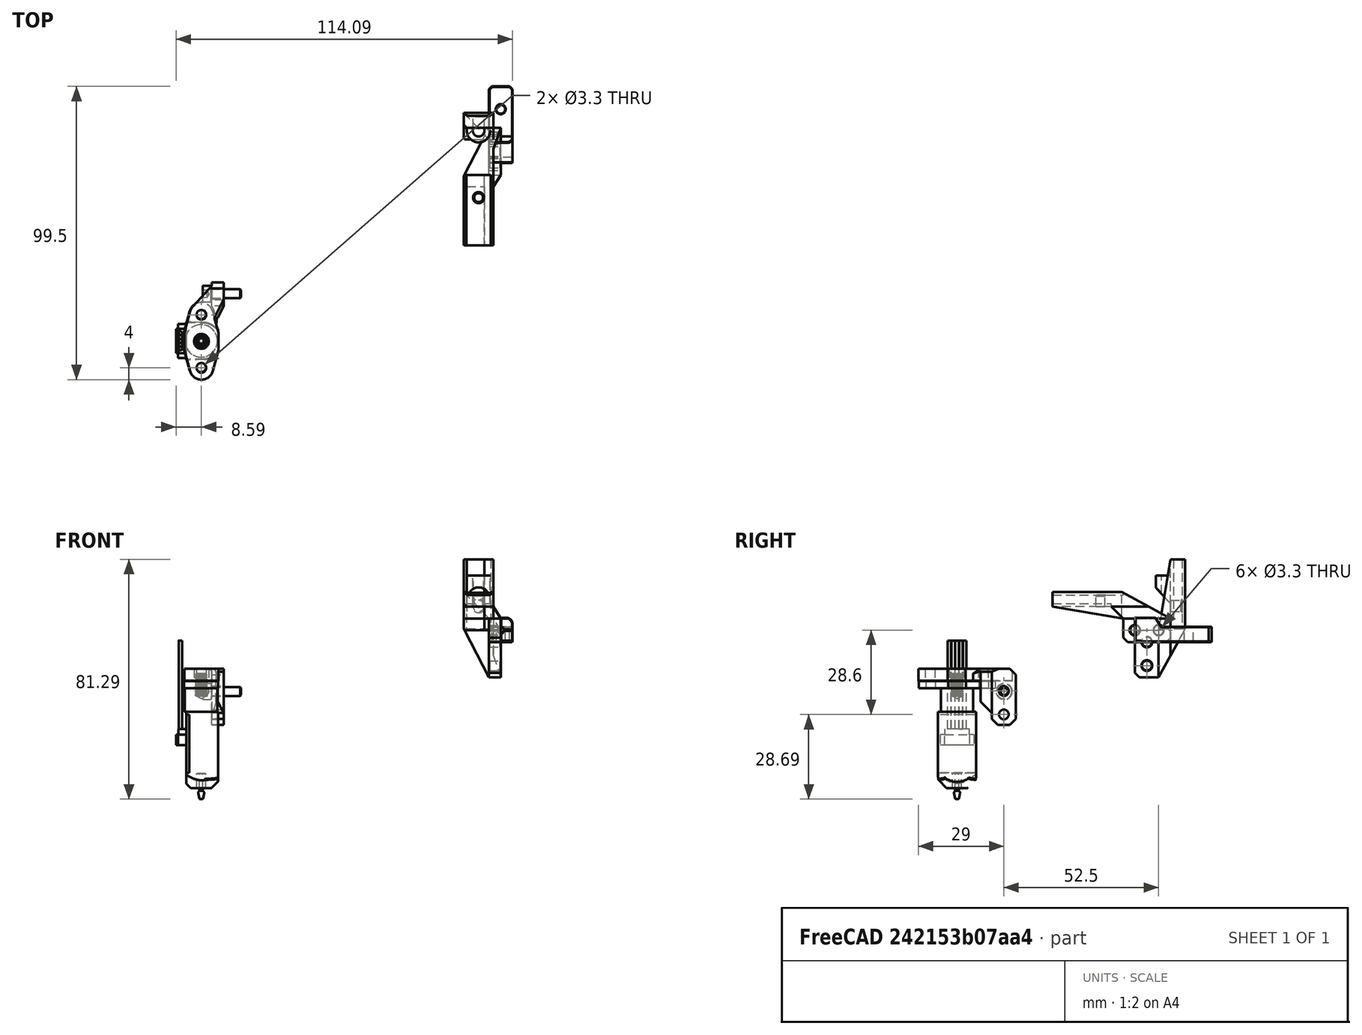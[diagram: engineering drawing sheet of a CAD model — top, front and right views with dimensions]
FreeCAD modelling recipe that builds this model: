
FCSTD DOCUMENT  (FreeCAD 0.19R24291 (Git))
Label: probe-mount-GXH8B
License: Other
LicenseURL: GPL3
objects: Part::Chamfer×18, Part::Box×14, Part::Cut×11, Part::Cylinder×5, Part::MultiFuse×5, Part::Feature×4, Part::FeaturePython×2, Part::Fillet×1, App::Part×1, Part::Refine×1
note: 61 computed .brp shape members not serialized (recipe doc carries the construction recipe); baked Part::Feature solids carry a one-line shape summary decoded from their .brp

FEATURE [Part::Box] Box  label="Cube"
  AttacherType = Attacher::AttachEngine3D
  Height = 8.2
  Length = 8
  Width = 9
FEATURE [Part::Box] Box001  label="Cube001"
  AttacherType = Attacher::AttachEngine3D
  Height = 5.2
  Length = 8
  Placement = pos=(0,8,0) rot=(0,0,1;0rad)
  Width = 18
FEATURE [Part::Box] Box002  label="Cube002"
  AttacherType = Attacher::AttachEngine3D
  Height = 0.2
  Length = 8
  Width = 2
FEATURE [Part::Cylinder] Cylinder
  Angle = 360
  AttacherType = Attacher::AttachEngine3D
  Height = 10
  Placement = pos=(4,18.25,0) rot=(0,0,1;0rad)
  Radius = 1.5
FEATURE [Part::Cylinder] Cylinder001
  Angle = 360
  AttacherType = Attacher::AttachEngine3D
  Height = 10
  Placement = pos=(4,0.25,4) rot=(1,0,0;1.5708rad)
  Radius = 1
FEATURE [Part::Box] Box003  label="Cube003"
  AttacherType = Attacher::AttachEngine3D
  Height = 2
  Length = 0.4
  Placement = pos=(3.8,0,0.5) rot=(0,0,1;0rad)
  Width = 0.25
FEATURE [Part::Box] Box004  label="Cube004"
  AttacherType = Attacher::AttachEngine3D
  Height = 2
  Length = 0.4
  Placement = pos=(3.8,0,5.5) rot=(0,0,1;0rad)
  Width = 0.25
FEATURE [Part::MultiFuse] Fusion001
  Shapes = -> [Box003,Box004]
FEATURE [Part::Feature] Fusion001001
  Placement = pos=(-1.8e-15,0,8) rot=(0,1,0;1.5708rad)
  shape: bbox 7 x 0.25 x 0.4 mm, 12 faces, 2 solids (baked)
FEATURE [Part::MultiFuse] Fusion001002
  Shapes = -> [Fusion001,Fusion001001]
FEATURE [Part::Cylinder] Cylinder002
  Angle = 360
  AttacherType = Attacher::AttachEngine3D
  Height = 10
  Placement = pos=(-1e-15,0,4) rot=(0,1,0;1.5708rad)
  Radius = 1.65
FEATURE [Part::Cylinder] Cylinder003
  Angle = 360
  AttacherType = Attacher::AttachEngine3D
  Height = 10
  Placement = pos=(-1e-15,8,4) rot=(0,1,0;1.5708rad)
  Radius = 1.65
FEATURE [Part::Box] Box007  label="Cube007"
  AttacherType = Attacher::AttachEngine3D
  Height = 8
  Length = 4
  Placement = pos=(0,-4,0) rot=(0,0,1;0rad)
  Width = 16
FEATURE [Part::Box] Box008  label="Cube008"
  AttacherType = Attacher::AttachEngine3D
  Height = 9
  Length = 12.5
  Placement = pos=(-8.5,-8,8) rot=(0,0,1;0rad)
  Width = 20
FEATURE [Part::Box] Box009  label="Cube009"
  AttacherType = Attacher::AttachEngine3D
  Height = 5
  Length = 10
  Placement = pos=(-8.5,-28,12) rot=(0,0,1;0rad)
  Width = 23.5
FEATURE [Part::Box] Box010  label="Cube010"
  AttacherType = Attacher::AttachEngine3D
  Height = 10
  Length = 12.5
  Placement = pos=(1.5,-9.5,8) rot=(0,0,1;0rad)
  Width = 21.5
FEATURE [Part::Chamfer] Chamfer009
  Base = -> Box010
  Edges = 1 edges: [Edge4 r1=4 r2=2.5]
FEATURE [Part::Chamfer] Chamfer010
  Base = -> Box008
  Edges = 1 edges r=4: [Edge9]
FEATURE [Part::Cut] Cut003001002
  Base = -> Chamfer010
  Tool = -> Chamfer009
FEATURE [Part::Chamfer] Chamfer011
  Base = -> Box007
  Edges = 2 edges r=1.5: [Edge9,Edge11]
FEATURE [Part::MultiFuse] Fusion001003
  Shapes = -> [Cylinder003,Cylinder002]
FEATURE [Part::Cut] Cut003001003
  Base = -> Chamfer011
  Tool = -> Fusion001003
FEATURE [Part::Box] Box011  label="Cube011"
  AttacherType = Attacher::AttachEngine3D
  Height = 5
  Length = 8.2
  Placement = pos=(-7.6,-28.5,16) rot=(0,0,1;0rad)
  Width = 24
FEATURE [Part::Chamfer] Chamfer012
  Base = -> Cut003001002
  Edges = 1 edges: [Edge4 r1=16.5 r2=8.5]
FEATURE [Part::Box] Box012  label="Cube012"
  AttacherType = Attacher::AttachEngine3D
  Height = 17
  Length = 15
  Placement = pos=(-10.8,-4.5,8) rot=(0,0,1;0rad)
  Width = 21
FEATURE [Part::Chamfer] Chamfer013
  Base = -> Box012
  Edges = 1 edges: [Edge9 r1=9 r2=16.5]
FEATURE [Part::Cut] Cut003001004
  Base = -> Chamfer012
  Tool = -> Chamfer013
FEATURE [Part::Box] Box013  label="Cube013"
  AttacherType = Attacher::AttachEngine3D
  Height = 5
  Length = 3
  Placement = pos=(-1.5,-3.5,13) rot=(1,0,0;3.14159rad)
  Width = 24.5
FEATURE [Part::Cylinder] Cylinder004
  Angle = 360
  AttacherType = Attacher::AttachEngine3D
  Height = 10
  Placement = pos=(-3.5,-12.25,10) rot=(0,0,1;0rad)
  Radius = 1.9
FEATURE [Part::Cut] Cut
  Base = -> Box
  Tool = -> Box002
FEATURE [Part::Chamfer] Chamfer
  Base = -> Cut
  Edges = 1 edges: [Edge10 r1=2 r2=3]
FEATURE [Part::Fillet] Fillet
  Base = -> Chamfer
  Edges = 2 edges r=2: [Edge1,Edge9]
FEATURE [Part::Chamfer] Chamfer001
  Base = -> Fillet
  Edges = 2 edges r=0.2: [Edge2,Edge16]
FEATURE [Part::Chamfer] Chamfer002
  Base = -> Chamfer001
  Edges = 2 edges r=0.2: [Edge5,Edge31]
FEATURE [Part::Cut] Cut001
  Base = -> Chamfer002
  Tool = -> Cylinder001
FEATURE [Part::Chamfer] Chamfer005
  Base = -> Cut001
  Edges = 9 edges r=0.2: [Edge4,Edge17,Edge19,Edge20,Edge21,Edge22,Edge23,Edge24,Edge25]
FEATURE [Part::Chamfer] Chamfer006
  Base = -> Chamfer005
  Edges = 5 edges r=0.2: [Edge7,Edge9,Edge14,Edge15,Edge16]
FEATURE [Part::Cut] Cut003001008
  Base = -> Chamfer006
  Tool = -> Fusion001002
FEATURE [Part::Feature] Part__Feature112001139  label="BL-touch v3.x002"
  Placement = pos=(-97.5942,-60.3565,-13.2887) rot=(0,0,1;1.5708rad)
  shape: bbox 16.53 x 26.01 x 53.81 mm, 111 faces (baked)
FEATURE [Part::FeaturePython] Screw1371  label="M3x10-Screw189"  # Fasteners workbench fastener (typed FeaturePython)
  Placement = pos=(-94.0942,-44.3565,-16.7887) rot=(0,-1,0;1.5708rad)
  diameter = 4
  invert = false
  length = 10
  lengthCustom = 10
  matchOuter = true
  offset = 0
  thread = false
  type = 33
FEATURE [Part::Feature] Part__Feature  label="bltouch-mount"
  Placement = pos=(-69.5,-39.5,-13.1) rot=(0,0,1;0rad)
  shape: bbox 13.25 x 33 x 19 mm, 31 faces (baked)
FEATURE [App::Part] BL_Touch__1_001  label="BL-Touch <1>001"
  Group = -> [Part__Feature112001139,Screw1371,Part__Feature]
  Origin = -> Origin206
  Placement = pos=(70,24.5,-40.5) rot=(1,0,0;4.71239rad)
FEATURE [Part::Chamfer] Chamfer021
  Base = -> Box001
  Edges = 2 edges r=1: [Edge3,Edge7]
FEATURE [Part::Chamfer] Chamfer022
  Base = -> Chamfer021
  Edges = 12 edges r=0.2: [Edge1,Edge3,Edge5,Edge6,Edge7,Edge8,Edge9,Edge10,Edge12,Edge14,Edge15,Edge16]
FEATURE [Part::MultiFuse] Fusion
  Shapes = -> [Chamfer022,Cut003001008]
FEATURE [Part::Chamfer] Chamfer023003
  Base = -> Box009
  Edges = 2 edges r=1: [Edge4,Edge8]
FEATURE [Part::Chamfer] Chamfer023004
  Base = -> Box013
  Edges = 1 edges: [Edge12 r1=4 r2=24]
FEATURE [Part::MultiFuse] Fusion001004
  Shapes = -> [Cut003001003,Cut003001004,Chamfer023004,Chamfer023003]
FEATURE [Part::Cut] Cut003001014
  Base = -> Fusion
  Refine = true
  Tool = -> Cylinder
FEATURE [Part::Chamfer] Chamfer023007
  Base = -> Cut003001014
  Edges = 2 edges r=0.2: [Edge70,Edge133]
FEATURE [Part::Feature] Chamfer023006001  label="old"
  shape: bbox 12.5 x 40 x 17 mm, 46 faces (baked)
FEATURE [Part::Cut] Cut003001015
  Base = -> Fusion001004
  Tool = -> Box011
FEATURE [Part::Cut] Cut003001016
  Base = -> Cut003001015
  Tool = -> Cylinder004
FEATURE [Part::Chamfer] Chamfer023006002
  Base = -> Cut003001016
  Edges = 1 edges r=0.4: [Edge92]
FEATURE [Part::Chamfer] Chamfer023006003
  Base = -> Chamfer023006002
  Edges = 4 edges r=0.2: [Edge73,Edge74,Edge96,Edge98]
FEATURE [Part::Refine] Chamfer023006003001
  Placement = pos=(0,0,0) rot=(-1,0,0;1.5708rad)
  Source = -> Chamfer023006003
FEATURE [Part::FeaturePython] Tube  # WARN: FeaturePython — macro-defined, semantics opaque (R4)
  AttacherType = Attacher::AttachEngine3D
  Height = 10
  InnerRadius = 2
  OuterRadius = 4
  Placement = pos=(-3.5,11,12) rot=(0,0,1;0rad)
FEATURE [Part::Box] Box014  label="Cube014"
  AttacherType = Attacher::AttachEngine3D
  Height = 19
  Length = 10
  Placement = pos=(-10.5,0,0) rot=(0,0,1;0rad)
  Width = 10
FEATURE [Part::Chamfer] Chamfer023006003002
  Base = -> Box014
  Edges = 1 edges: [Edge12 r1=10 r2=9]
  Placement = pos=(2,2,3.5) rot=(0,0,1;0rad)
FEATURE [Part::Cut] Cut003001017
  Base = -> Tube
  Tool = -> Chamfer023006003002
FEATURE [Part::Box] Box015  label="Cube015"
  AttacherType = Attacher::AttachEngine3D
  Height = 19
  Length = 10
  Placement = pos=(-8.5,12,8.5) rot=(0,0,1;0rad)
  Width = 10
FEATURE [Part::Cut] Cut003001018
  Base = -> Cut003001017
  Placement = pos=(0,0,0.5) rot=(0,0,1;0rad)
  Tool = -> Box015
